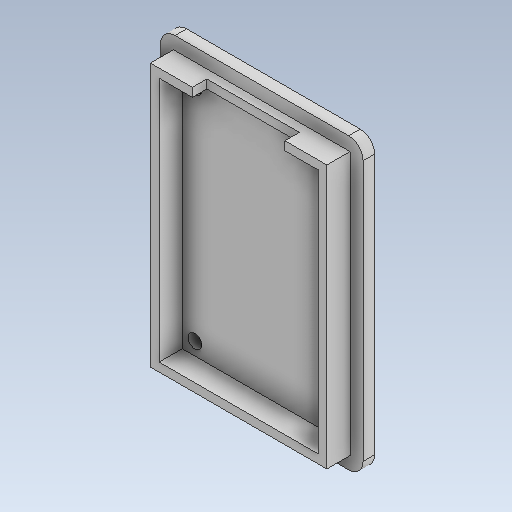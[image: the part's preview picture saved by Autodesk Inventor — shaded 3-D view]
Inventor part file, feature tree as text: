
AUTODESK INVENTOR PART (.ipt)
format: ipt  version: 2020 (Build 240168000, 168)  size: 169,472 bytes
history: native  units: in
note: dims shown in document units (in); Inventor stores cm internally (conversion verified against a paired STEP export)
features: extrude x5, sketch x5, fillet x1
ambient origin geometry x8: Origin, YZ Plane, XZ Plane, XY Plane, X Axis, Y Axis, Z Axis, Center Point
bodies: Solid1 (feature_tree)
feature tree (11):
  extrude  "Extrusion1"  Depth=5.0in
  fillet  "Fillet1"  Radius=0.2in
  extrude  "Extrusion2"  Depth=3.05in
  extrude  "Extrusion3"  Depth=0.4in TaperAngle=0.0deg
  extrude  "Extrusion4"  Depth=0.15in
  extrude  "Extrusion5"  Depth=1.6in
  sketch  "Sketch1"  dims[d0=3.5in d1=5.0in d2=0.2in d3=0.0in]
  sketch  "Sketch2"  dims[d4=0.25in d5=3.05in]
  sketch  "Sketch3"  dims[d6=4.55in d7=0.4in d8=0.0in]
  sketch  "Sketch4"  dims[d9=0.15in d10=0.15in]
  sketch  "Sketch5"  dims[d11=0.4in d12=0.0in d13=1.6in d14=0.25in d15=0.4in d16=0.0in d17=0.2362in d18=0.2205in d19=0.2205in d20=0.3937in d21=0.0in]
